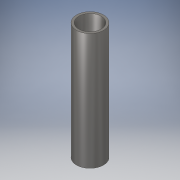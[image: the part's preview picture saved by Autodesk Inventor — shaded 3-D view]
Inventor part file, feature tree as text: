
AUTODESK INVENTOR PART (.ipt)
format: ipt  version: 2019 (Build 230136000, 136)  size: 101,376 bytes
history: native  units: mm
features: extrude x1, sketch x1
ambient origin geometry x8: Origin, YZ Plane, XZ Plane, XY Plane, X Axis, Y Axis, Z Axis, Center Point
bodies: Solid1 (feature_tree)
feature tree (2):
  extrude  "Extrusion1"  Depth=10.0mm
  sketch  "Sketch1"  dims[d0=12.0mm d1=10.0mm d2=52.0mm d3=0.0mm]
